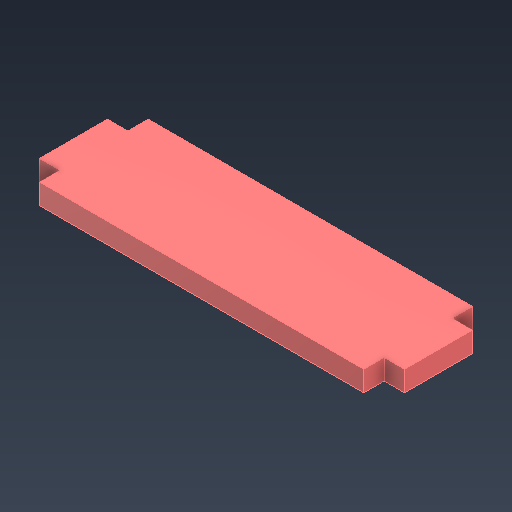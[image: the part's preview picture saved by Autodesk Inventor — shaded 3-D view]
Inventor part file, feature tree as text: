
AUTODESK INVENTOR PART (.ipt)
format: ipt  version: 2025.3 (Build 293356000, 356)  size: 100,352 bytes
history: native  units: mm
features: other x1, extrude x1, sketch x1
ambient origin geometry x8: Origin, YZ Plane, XZ Plane, XY Plane, X Axis, Y Axis, Z Axis, Center Point
bodies: Body1 (feature_tree)
feature tree (3):
  other  "實體1"
  extrude  "擠出1"  Depth=10.0mm
  sketch  "草圖1"
